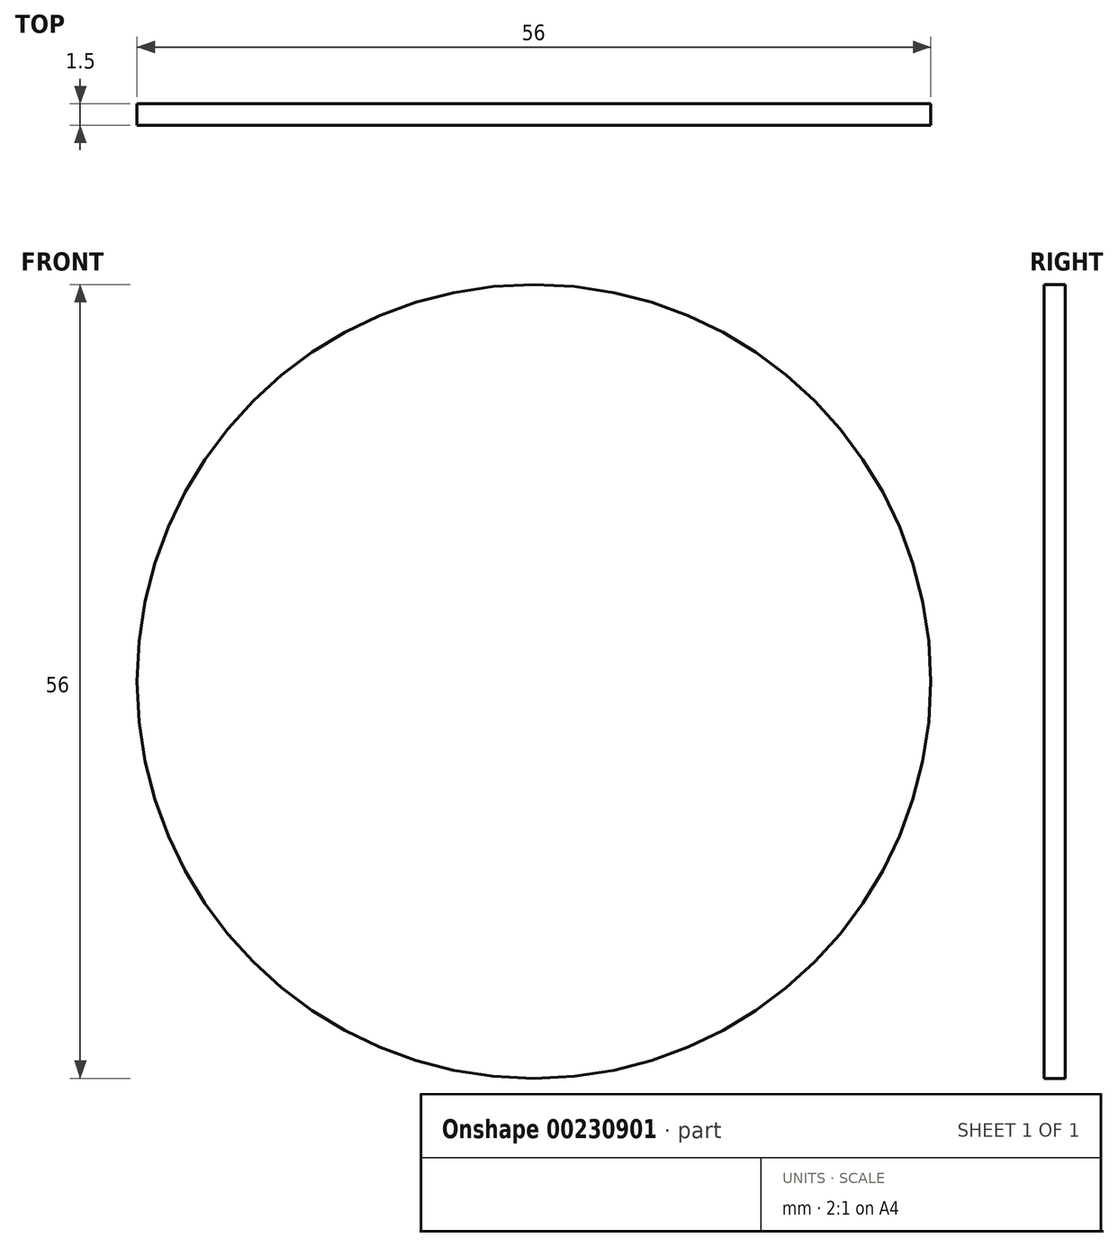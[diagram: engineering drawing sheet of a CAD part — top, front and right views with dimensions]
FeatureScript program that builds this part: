
annotation { "Feature Type Name" : "Feature", "Feature Type Description" : "" }
export const myFeature = defineFeature(function(context is Context, id is Id, definition is map)
    precondition{}
    {
        {
            var Q0;
            Q0=qCreatedBy(makeId("Front.planeOp"),FACE);
            var sketch = newSketch(context, id + "F0", { "sketchPlane" : qUnion([Q0])});
            skCircle(sketch, "E0", {"center": v(0, 0) * mm, "radius": 28 * mm});
            skSolve(sketch);
        }
        {
            var Q0;
            Q0 = qSketchRegion(id + "F0", true);
            var Q1;
            Q1=sQuery(id+"F0.wireOp",EDGE,"E0");
            extrude(context, id + "F1", {"entities" : qUnion([Q0]), "surfaceEntities" : qUnion([Q1]), "endBound" : BoundingType.SYMMETRIC, "depth" : 1.5 * mm});
        }
    });
